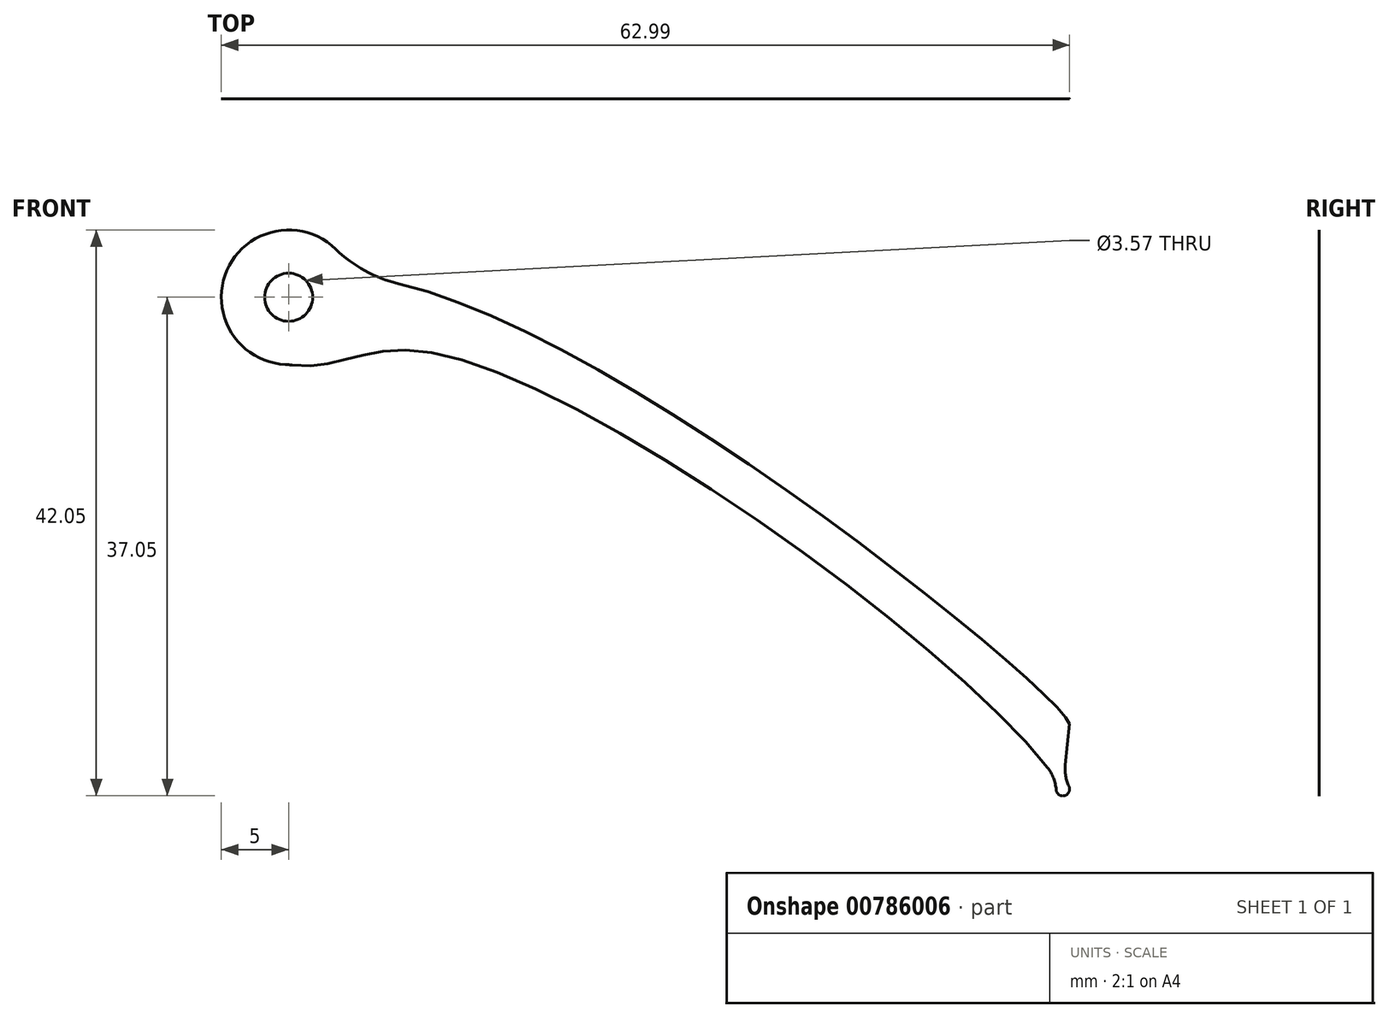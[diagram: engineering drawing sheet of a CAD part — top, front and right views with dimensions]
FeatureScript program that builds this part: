
annotation { "Feature Type Name" : "Feature", "Feature Type Description" : "" }
export const myFeature = defineFeature(function(context is Context, id is Id, definition is map)
    precondition{}
    {
        {
            var Q0;
            Q0=qCreatedBy(makeId("Front.planeOp"),FACE);
            var sketch = newSketch(context, id + "F0", { "sketchPlane" : qUnion([Q0])});
            skCircle(sketch, "E0", {"center": v(0, 0) * mm, "radius": 1.79 * mm});
            skCircle(sketch, "E1", {"center": v(0, 0) * mm, "radius": 5 * mm});
            skFitSpline(sketch, "E2", {"points": [v(0, 0) * mm, v(28.9, -8.94) * mm, v(57.98, -31.7) * mm], "startDerivative": vector(25.87, 26.74) * mm, "endDerivative": vector(2.76, -9.67) * mm});
            skFitSpline(sketch, "E3", {"points": [v(0, -5) * mm, v(11.08, -4.2) * mm, v(57.5, -36.55) * mm], "startDerivative": vector(35.12, -6.69) * mm, "endDerivative": vector(24.21, -38.97) * mm});
            skLineSegment(sketch, "E4", {"start": v(57.98, -31.7) * mm, "end": v(57.5, -36.55) * mm});
            skCircle(sketch, "E5", {"center": v(57.5, -36.55) * mm, "radius": 0.5 * mm});
            skSolve(sketch);
        }
        {
            var Q0;
            Q0=qSketchRegion(id+"F0",true);
            extrude(context, id + "F1", {"entities" : qUnion([Q0]), "depth" : 1 / 203.2 * mm, "offsetDistance" : 25 * mm});
        }
        {
            var Q0;
            Q0=makeQuery(id+"F1.opExtrude","SWEPT_EDGE",EDGE,{"disambiguationData":[OSD([sQuery(id+"F0.wireOp",EDGE,"E1"),sQuery(id+"F0.wireOp",EDGE,"E2")])]});
            fillet(context, id + "F2", {"entities" : qUnion([Q0]), "radius" : 10 * mm, "tangentPropagation" : true, "allowEdgeOverflow" : false});
        }
        {
            var Q0;
            Q0=makeQuery(id+"F1.opExtrude","SWEPT_EDGE",EDGE,{"disambiguationData":[OSD([sQuery(id+"F0.wireOp",EDGE,"E1"),sQuery(id+"F0.wireOp",EDGE,"E3")])]});
            fillet(context, id + "F3", {"entities" : qUnion([Q0]), "radius" : 5 * mm, "tangentPropagation" : true, "allowEdgeOverflow" : false});
        }
        {
            var Q0;
            Q0=makeQuery(id+"F1.opExtrude","SWEPT_EDGE",EDGE,{"disambiguationData":[OSD([sQuery(id+"F0.wireOp",EDGE,"E4"),sQuery(id+"F0.wireOp",EDGE,"E5")])]});
            var Q1;
            Q1=makeQuery(id+"F1.opExtrude","SWEPT_EDGE",EDGE,{"disambiguationData":[OSD([sQuery(id+"F0.wireOp",EDGE,"E3"),sQuery(id+"F0.wireOp",EDGE,"E5")])]});
            fillet(context, id + "F4", {"entities" : qUnion([Q0, Q1]), "radius" : 3 * mm, "tangentPropagation" : true, "allowEdgeOverflow" : false});
        }
    });
